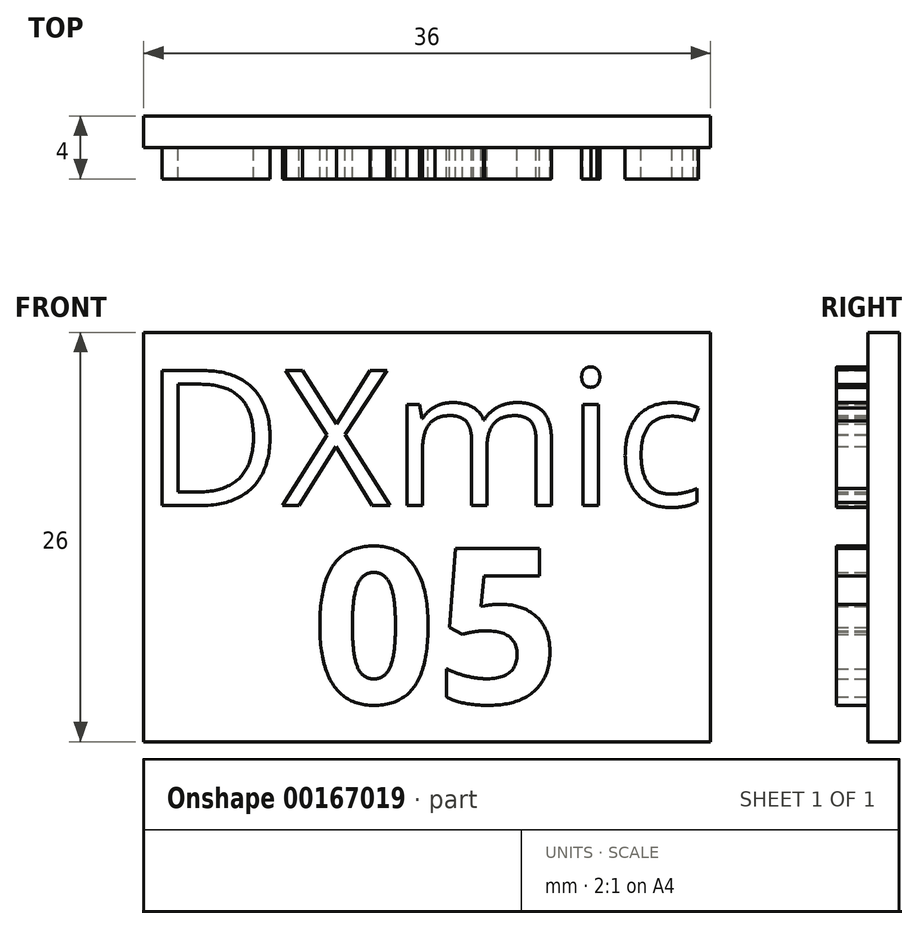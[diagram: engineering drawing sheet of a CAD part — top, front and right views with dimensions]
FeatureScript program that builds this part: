
annotation { "Feature Type Name" : "Feature", "Feature Type Description" : "" }
export const myFeature = defineFeature(function(context is Context, id is Id, definition is map)
    precondition{}
    {
        {
            var Q0;
            Q0=qCreatedBy(makeId("Front.planeOp"),FACE);
            var sketch = newSketch(context, id + "F0", { "sketchPlane" : qUnion([Q0])});
            skLineSegment(sketch, "E0", {"start": v(0, 0) * mm, "end": v(-36, 0) * mm});
            skLineSegment(sketch, "E1", {"start": v(-36, 0) * mm, "end": v(-36, 26) * mm});
            skLineSegment(sketch, "E2", {"start": v(-36, 26) * mm, "end": v(0, 26) * mm});
            skLineSegment(sketch, "E3", {"start": v(0, 26) * mm, "end": v(0, 0) * mm});
            skText(sketch, "E4", { "text": "DXmic", "fontName": "OpenSans-Regular.ttf"});
            skText(sketch, "E5", { "text": "05", "fontName": "OpenSans-Bold.ttf"});
            const initialGuessF0  = {"E4": [-0.036, 0.01499, 1, 0, 0.00865], "E5": [-0.02531, 0.00244, 1, 0, 0.00992]};
            skSetInitialGuess(sketch, initialGuessF0);
            skSolve(sketch);
        }
        {
            var Q0;
            Q0 = qSketchRegion(id + "F0", true);
            var Q1;
            Q1=makeQuery(id+"F0.imprint","IMPRINT",FACE,{"disambiguationData":[TD([[makeQuery(id+"F0.imprint","IMPRINT",EDGE,{"derivedFrom":sQuery(id+"F0.wireOp",EDGE,"E4.sketch_text.stroke-0")}),-1.0]])]});
            var Q2;
            Q2=makeQuery(id+"F0.imprint","IMPRINT",FACE,{"disambiguationData":[TD([[makeQuery(id+"F0.imprint","IMPRINT",EDGE,{"derivedFrom":sQuery(id+"F0.wireOp",EDGE,"E4.sketch_text.stroke-7")}),1.0]])]});
            var Q3;
            Q3=makeQuery(id+"F0.imprint","IMPRINT",FACE,{"disambiguationData":[TD([[makeQuery(id+"F0.imprint","IMPRINT",EDGE,{"derivedFrom":sQuery(id+"F0.wireOp",EDGE,"E4.sketch_text.stroke-14")}),-1.0]])]});
            var Q4;
            Q4=makeQuery(id+"F0.imprint","IMPRINT",FACE,{"disambiguationData":[TD([[makeQuery(id+"F0.imprint","IMPRINT",EDGE,{"derivedFrom":sQuery(id+"F0.wireOp",EDGE,"E5.sketch_text.stroke-0")}),-1.0]])]});
            var Q5;
            Q5=makeQuery(id+"F0.imprint","IMPRINT",FACE,{"disambiguationData":[TD([[makeQuery(id+"F0.imprint","IMPRINT",EDGE,{"derivedFrom":sQuery(id+"F0.wireOp",EDGE,"E5.sketch_text.stroke-8")}),1.0]])]});
            var Q6;
            Q6=makeQuery(id+"F0.imprint","IMPRINT",FACE,{"disambiguationData":[TD([[makeQuery(id+"F0.imprint","IMPRINT",EDGE,{"derivedFrom":sQuery(id+"F0.wireOp",EDGE,"E5.sketch_text.stroke-16")}),-1.0]])]});
            var Q7;
            Q7=makeQuery(id+"F0.imprint","IMPRINT",FACE,{"disambiguationData":[TD([[makeQuery(id+"F0.imprint","IMPRINT",EDGE,{"derivedFrom":sQuery(id+"F0.wireOp",EDGE,"E4.sketch_text.stroke-26")}),-1.0]])]});
            var Q8;
            Q8=makeQuery(id+"F0.imprint","IMPRINT",FACE,{"disambiguationData":[TD([[makeQuery(id+"F0.imprint","IMPRINT",EDGE,{"derivedFrom":sQuery(id+"F0.wireOp",EDGE,"E4.sketch_text.stroke-54")}),-1.0]])]});
            var Q9;
            Q9=makeQuery(id+"F0.imprint","IMPRINT",FACE,{"disambiguationData":[TD([[makeQuery(id+"F0.imprint","IMPRINT",EDGE,{"derivedFrom":sQuery(id+"F0.wireOp",EDGE,"E4.sketch_text.stroke-66")}),-1.0]])]});
            var Q10;
            Q10=makeQuery(id+"F0.imprint","IMPRINT",FACE,{"disambiguationData":[TD([[makeQuery(id+"F0.imprint","IMPRINT",EDGE,{"derivedFrom":sQuery(id+"F0.wireOp",EDGE,"E4.sketch_text.stroke-58")}),-1.0]])]});
            var Q11;
            Q11=makeQuery(id+"F0.imprint","IMPRINT",FACE,{"disambiguationData":[TD([[makeQuery(id+"F0.imprint","IMPRINT",EDGE,{"derivedFrom":sQuery(id+"F0.wireOp",EDGE,"E5.sketch_text.stroke-27")}),1.0]])]});
            extrude(context, id + "F1", {"entities" : qUnion([Q0, Q1, Q2, Q3, Q4, Q5, Q6, Q7, Q8, Q9, Q10, Q11]), "oppositeDirection" : true, "depth" : 2 * mm, "offsetDistance" : 25 * mm});
        }
        {
            var Q0;
            Q0=makeQuery(id+"F0.imprint","IMPRINT",FACE,{"disambiguationData":[TD([[makeQuery(id+"F0.imprint","IMPRINT",EDGE,{"derivedFrom":sQuery(id+"F0.wireOp",EDGE,"E4.sketch_text.stroke-66")}),-1.0]])]});
            var Q1;
            Q1=makeQuery(id+"F0.imprint","IMPRINT",FACE,{"disambiguationData":[TD([[makeQuery(id+"F0.imprint","IMPRINT",EDGE,{"derivedFrom":sQuery(id+"F0.wireOp",EDGE,"E4.sketch_text.stroke-54")}),-1.0]])]});
            var Q2;
            Q2=makeQuery(id+"F0.imprint","IMPRINT",FACE,{"disambiguationData":[TD([[makeQuery(id+"F0.imprint","IMPRINT",EDGE,{"derivedFrom":sQuery(id+"F0.wireOp",EDGE,"E4.sketch_text.stroke-58")}),-1.0]])]});
            var Q3;
            Q3=makeQuery(id+"F0.imprint","IMPRINT",FACE,{"disambiguationData":[TD([[makeQuery(id+"F0.imprint","IMPRINT",EDGE,{"derivedFrom":sQuery(id+"F0.wireOp",EDGE,"E4.sketch_text.stroke-26")}),-1.0]])]});
            var Q4;
            Q4=makeQuery(id+"F0.imprint","IMPRINT",FACE,{"disambiguationData":[TD([[makeQuery(id+"F0.imprint","IMPRINT",EDGE,{"derivedFrom":sQuery(id+"F0.wireOp",EDGE,"E4.sketch_text.stroke-14")}),-1.0]])]});
            var Q5;
            Q5=makeQuery(id+"F0.imprint","IMPRINT",FACE,{"disambiguationData":[TD([[makeQuery(id+"F0.imprint","IMPRINT",EDGE,{"derivedFrom":sQuery(id+"F0.wireOp",EDGE,"E4.sketch_text.stroke-0")}),-1.0]])]});
            var Q6;
            Q6=makeQuery(id+"F0.imprint","IMPRINT",FACE,{"disambiguationData":[TD([[makeQuery(id+"F0.imprint","IMPRINT",EDGE,{"derivedFrom":sQuery(id+"F0.wireOp",EDGE,"E5.sketch_text.stroke-0")}),-1.0]])]});
            var Q7;
            Q7=makeQuery(id+"F0.imprint","IMPRINT",FACE,{"disambiguationData":[TD([[makeQuery(id+"F0.imprint","IMPRINT",EDGE,{"derivedFrom":sQuery(id+"F0.wireOp",EDGE,"E5.sketch_text.stroke-16")}),-1.0]])]});
            extrude(context, id + "F2", {"entities" : qUnion([Q0, Q1, Q2, Q3, Q4, Q5, Q6, Q7]), "operationType" : NewBodyOperationType.ADD, "depth" : 2 * mm, "offsetDistance" : 25 * mm});
        }
    });
